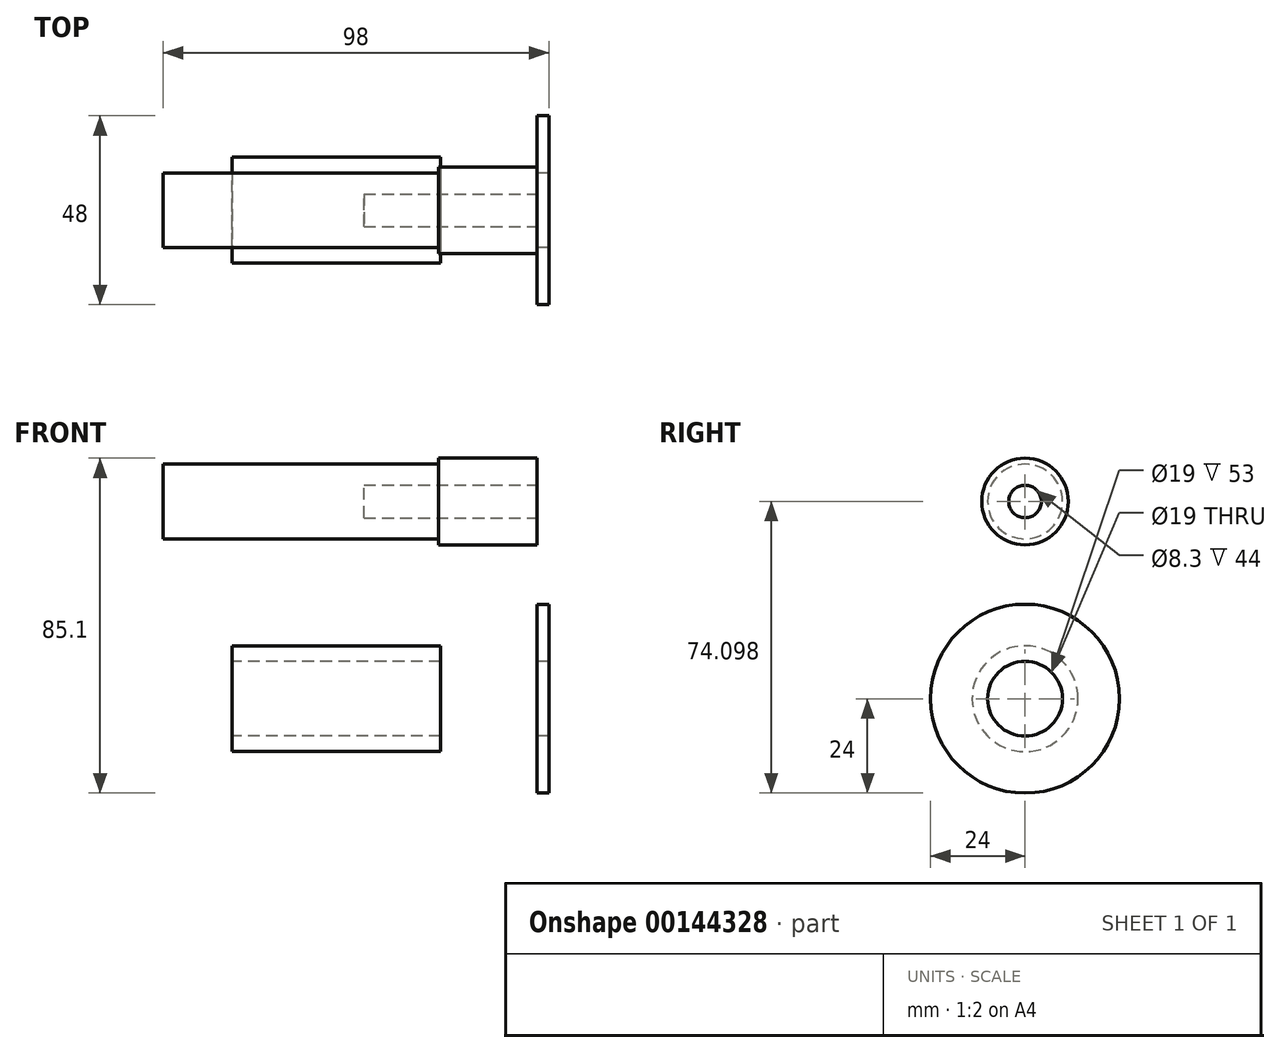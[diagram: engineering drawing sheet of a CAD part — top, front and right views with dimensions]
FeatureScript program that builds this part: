
annotation { "Feature Type Name" : "Feature", "Feature Type Description" : "" }
export const myFeature = defineFeature(function(context is Context, id is Id, definition is map)
    precondition{}
    {
        {
            var Q0;
            Q0=qCreatedBy(makeId("Right.planeOp"),FACE);
            var sketch = newSketch(context, id + "F0", { "sketchPlane" : qUnion([Q0])});
            skCircle(sketch, "E0", {"center": v(0, 0) * mm, "radius": 9.5 * mm});
            skCircle(sketch, "E1", {"center": v(0, 0) * mm, "radius": 24 * mm});
            skSolve(sketch);
        }
        {
            var Q0;
            Q0 = qSketchRegion(id + "F0", true);
            extrude(context, id + "F1", {"entities" : qUnion([Q0]), "depth" : 3 * mm});
        }
        {
            var Q0;
            Q0=qCreatedBy(makeId("Front.planeOp"),FACE);
            var sketch = newSketch(context, id + "F2", { "sketchPlane" : qUnion([Q0])});
            skLineSegment(sketch, "E2", {"start": v(55.65, 0) * mm, "end": v(-77.5, 0) * mm, "construction": true});
            skSolve(sketch);
        }
        {
            var Q0;
            Q0=sQuery(id+"F2.wireOp",VERTEX,"E2.end");
            var Q1;
            Q1=qCreatedBy(makeId("Right.planeOp"),FACE);
            cPlane(context, id + "F3", {"entities" : qUnion([Q0, Q1]), "cplaneType" : CPlaneType.PLANE_POINT, "offset" : 25 * mm, "width" : 150 * mm, "height" : 150 * mm});
        }
        {
            var Q0;
            Q0=qCreatedBy(id+"F3.planeOp",FACE);
            var sketch = newSketch(context, id + "F4", { "sketchPlane" : qUnion([Q0])});
            skCircle(sketch, "E3", {"center": v(0, 0) * mm, "radius": 9.5 * mm});
            skCircle(sketch, "E4", {"center": v(0, 0) * mm, "radius": 13.45 * mm});
            skSolve(sketch);
        }
        {
            var Q0;
            Q0 = qSketchRegion(id + "F4", true);
            extrude(context, id + "F5", {"entities" : qUnion([Q0]), "depth" : 53 * mm});
        }
        {
            var Q0;
            Q0=qCreatedBy(makeId("Right.planeOp"),FACE);
            var sketch = newSketch(context, id + "F6", { "sketchPlane" : qUnion([Q0])});
            skCircle(sketch, "E5", {"center": v(0, 50.1) * mm, "radius": 11 * mm});
            skSolve(sketch);
        }
        {
            var Q0;
            Q0 = qSketchRegion(id + "F6", true);
            extrude(context, id + "F7", {"entities" : qUnion([Q0]), "oppositeDirection" : true, "depth" : 25 * mm});
        }
        {
            var Q0;
            Q0=makeQuery(id+"F7.opExtrude","CAP_FACE",FACE,{"disambiguationData":[OSD([sQuery(id+"F6.wireOp",EDGE,"E5")])],"isStart":false});
            var sketch = newSketch(context, id + "F8", { "sketchPlane" : qUnion([Q0])});
            skCircle(sketch, "E6", {"center": v(0, 50.1) * mm, "radius": 9.5 * mm});
            skSolve(sketch);
        }
        {
            var Q0;
            Q0 = qSketchRegion(id + "F8", true);
            extrude(context, id + "F9", {"entities" : qUnion([Q0]), "operationType" : NewBodyOperationType.ADD, "depth" : 70 * mm});
        }
        {
            var Q0;
            Q0=makeQuery(id+"F7.opExtrude","CAP_FACE",FACE,{"disambiguationData":[OSD([sQuery(id+"F6.wireOp",EDGE,"E5")])],"isStart":true});
            var sketch = newSketch(context, id + "F10", { "sketchPlane" : qUnion([Q0])});
            skCircle(sketch, "E7", {"center": v(0, 50.1) * mm, "radius": 4.15 * mm});
            skSolve(sketch);
        }
        {
            var Q0;
            Q0 = qSketchRegion(id + "F10", true);
            extrude(context, id + "F11", {"entities" : qUnion([Q0]), "operationType" : NewBodyOperationType.REMOVE, "oppositeDirection" : true, "depth" : 44 * mm});
        }
    });
